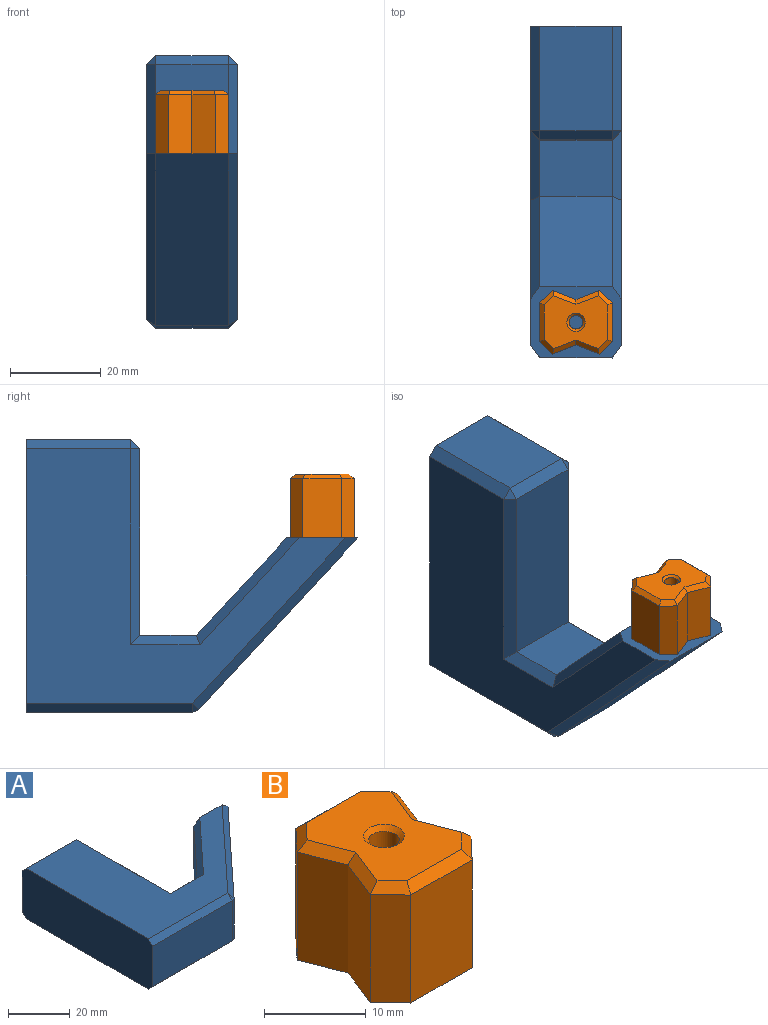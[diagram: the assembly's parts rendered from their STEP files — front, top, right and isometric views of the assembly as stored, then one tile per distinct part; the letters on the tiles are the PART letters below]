
ASSEMBLY  parts=2 mates=1
PART A: 28 faces, bbox 73x60x20 mm
  f0: plane 36.52x16mm, normal (0,-1,0), area 584.3mm2, adj f7,f21,f24,f25
  f1: plane 37.73x34.97mm, normal (0.73,-0.68,0), area 823mm2, adj f2,f22,f25,f27
  f2: plane 20x15.68mm, normal (0,1,0), area 302.8mm2, adj f1,f3,f8,f9,f10,f17,f22,f27
  f3: plane 21.45x19.88mm, normal (-0.73,0.68,0), area 467.8mm2, adj f2,f4,f10,f17
  f4: plane 16x12.39mm, normal (0,1,0), area 198.3mm2, adj f3,f5,f11,f19
  f5: plane 41.08x16mm, normal (1,0,0), area 657.3mm2, adj f4,f12,f15,f20
  f6: plane 23x16mm, normal (0,1,0), area 368mm2, adj f7,f13,f15,f16
  f7: plane 60x20mm, normal (-1,0,0), area 1192mm2, adj f0,f6,f8,f9,f13,f16,f21,f24
  f8: plane 70.23x56mm, normal (0,0,1), area 1779.9mm2, adj f2,f7,f10,f11,f12,f13,f21,f22
  f9: plane 70.23x56mm, normal (0,0,-1), area 1779.9mm2, adj f2,f7,f16,f17,f19,f20,f24,f27
  f10: plane 23.45x22.6mm, normal (-0.52,0.48,0.71), area 86.6mm2, adj f2,f3,f8,f11
  f11: plane 15.27x2mm, normal (0,0.71,0.71), area 39.1mm2, adj f4,f8,f10,f12
  f12: plane 43.08x2mm, normal (0.71,0,0.71), area 119mm2, adj f5,f8,f11,f14
  f13: plane 23x2mm, normal (0,0.71,0.71), area 65.1mm2, adj f6,f7,f8,f14
  f14: plane 2x2mm, normal (0.58,0.58,0.58), area 3.5mm2, adj f12,f13,f15
  f15: plane 16x2mm, normal (0.71,0.71,0), area 45.3mm2, adj f5,f6,f14,f18
  f16: plane 23x2mm, normal (0,0.71,-0.71), area 65.1mm2, adj f6,f7,f9,f18
  f17: plane 23.45x22.6mm, normal (-0.52,0.48,-0.71), area 86.6mm2, adj f2,f3,f9,f19
  f18: plane 2x2mm, normal (0.58,0.58,-0.58), area 3.5mm2, adj f15,f16,f20
  f19: plane 15.27x2mm, normal (0,0.71,-0.71), area 39.1mm2, adj f4,f9,f17,f20
  f20: plane 43.08x2mm, normal (0.71,0,-0.71), area 119mm2, adj f5,f9,f18,f19
  f21: plane 36.52x2mm, normal (0,-0.71,0.71), area 103.3mm2, adj f0,f7,f8,f23
  f22: plane 37.73x36.43mm, normal (0.52,-0.48,0.71), area 142.9mm2, adj f1,f2,f8,f23
  f23: plane 2x2mm, normal (0.3,-0.68,0.68), area 2.2mm2, adj f21,f22,f25
  f24: plane 36.52x2mm, normal (0,-0.71,-0.71), area 103.3mm2, adj f0,f7,f9,f26
  f25: plane 16x1.47mm, normal (0.4,-0.92,0), area 25.6mm2, adj f0,f1,f23,f26
  f26: plane 2x2mm, normal (0.3,-0.68,-0.68), area 2.2mm2, adj f24,f25,f27
  f27: plane 37.73x36.43mm, normal (0.52,-0.48,-0.71), area 142.9mm2, adj f1,f2,f9,f26
PART B: 24 faces, bbox 14x16x14 mm
  f0: plane 13x2.91mm, normal (-0.73,0.69,0), area 52mm2, adj f1,f9,f11,f12
  f1: plane 13x5.09mm, normal (-0.93,-0.37,0), area 71.1mm2, adj f0,f2,f11,f14
  f2: plane 13x5.09mm, normal (-0.93,0.37,0), area 71.1mm2, adj f1,f3,f11,f16
  f3: plane 13x2.91mm, normal (-0.73,-0.69,0), area 52mm2, adj f2,f4,f11,f18
  f4: plane 13x8.52mm, normal (0,-1,0), area 110.7mm2, adj f3,f5,f11,f20
  f5: plane 13x2.91mm, normal (0.73,-0.69,0), area 52mm2, adj f4,f6,f11,f21
  f6: plane 13x5.09mm, normal (0.93,0.37,0), area 71.1mm2, adj f5,f7,f11,f19
  f7: plane 13x5.09mm, normal (0.93,-0.37,0), area 71.1mm2, adj f6,f8,f11,f17
  f8: plane 13x2.91mm, normal (0.73,0.69,0), area 52mm2, adj f7,f9,f11,f15
  f9: plane 13x8.52mm, normal (0,1,0), area 110.7mm2, adj f0,f8,f11,f13
  f10: plane 14x11.68mm, normal (0,0,1), area 123.7mm2, adj f12,f13,f14,f15,f16,f17,f18,f19
  f11: plane 16x14mm, normal (0,0,-1), area 180.6mm2, adj f0,f1,f2,f3,f4,f5,f6,f7
  f12: plane 3.17x3.14mm, normal (-0.51,0.48,0.71), area 4.9mm2, adj f0,f10,f13,f14
  f13: plane 8.52x1mm, normal (0,0.71,0.71), area 11.4mm2, adj f9,f10,f12,f15
  f14: plane 5.09x3.07mm, normal (-0.66,-0.26,0.71), area 7.6mm2, adj f1,f10,f12,f16
  f15: plane 3.17x3.14mm, normal (0.51,0.48,0.71), area 4.9mm2, adj f8,f10,f13,f17
  f16: plane 5.09x3.07mm, normal (-0.66,0.26,0.71), area 7.6mm2, adj f2,f10,f14,f18
  f17: plane 5.09x3.07mm, normal (0.66,-0.26,0.71), area 7.6mm2, adj f7,f10,f15,f19
  f18: plane 3.17x3.14mm, normal (-0.51,-0.48,0.71), area 4.9mm2, adj f3,f10,f16,f20
  f19: plane 5.09x3.07mm, normal (0.66,0.26,0.71), area 7.6mm2, adj f6,f10,f17,f21
  f20: plane 8.52x1mm, normal (0,-0.71,0.71), area 11.4mm2, adj f4,f10,f18,f21
  f21: plane 3.17x3.14mm, normal (0.51,-0.48,0.71), area 4.9mm2, adj f5,f10,f19,f20
  f22: cylinder r=1.5mm len=13.5mm, axis (0,0,1), area 127.2mm2, adj f11,f23
  f23: cone r=1.5mm half-angle=45deg, axis (0,0,1), area 7.8mm2, adj f10,f22
PLACE A rot(axis=(0.58,-0.58,-0.58),120deg) t=(50.07,88.93,-1.99)mm
PLACE B rot(axis=(0,0,-1),90deg) t=(40.07,36.32,6.38)mm
MATE fastened A.f2 <-> B.f22  axis (0,0,1) through (40.07,36.32,6.38)mm
